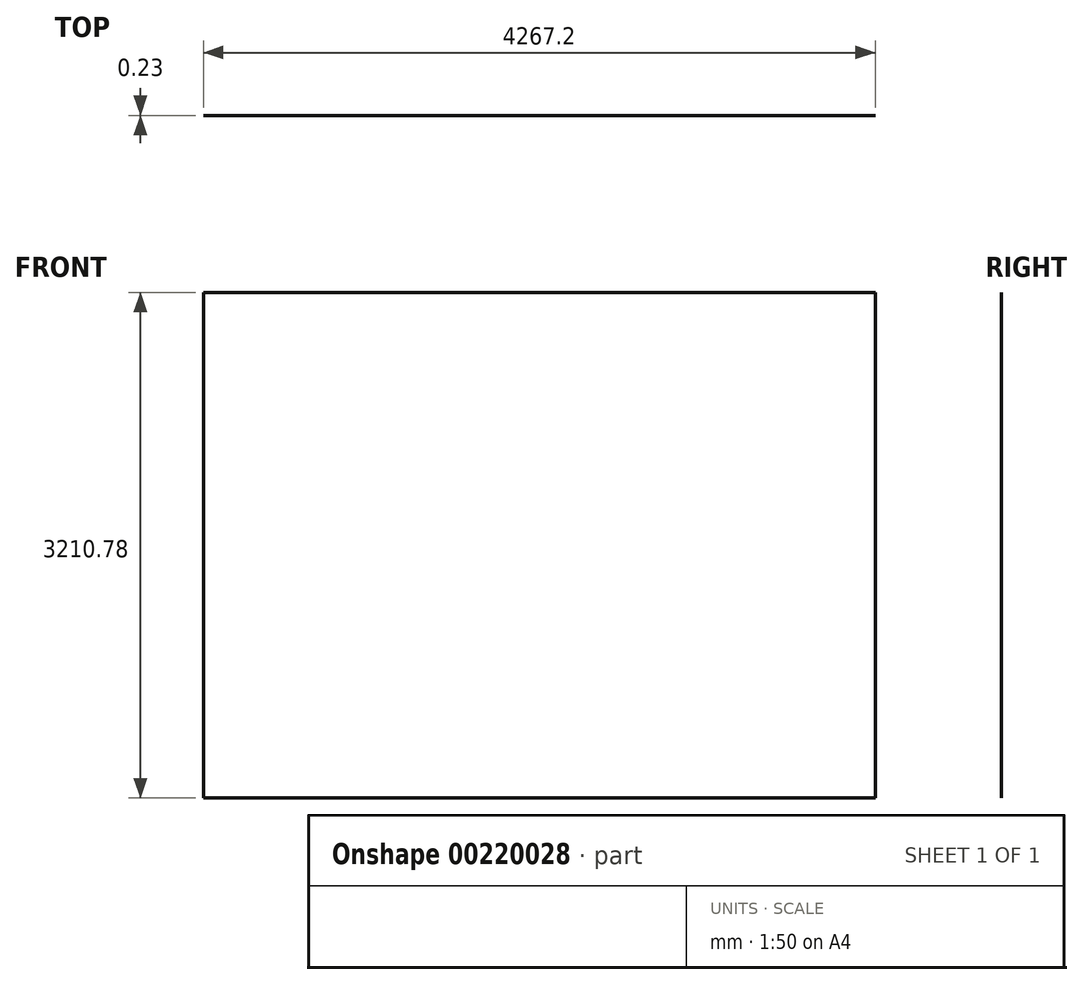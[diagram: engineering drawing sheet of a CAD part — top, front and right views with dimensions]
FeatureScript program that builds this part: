
annotation { "Feature Type Name" : "Feature", "Feature Type Description" : "" }
export const myFeature = defineFeature(function(context is Context, id is Id, definition is map)
    precondition{}
    {
        {
            var Q0;
            Q0=qCreatedBy(makeId("Front.planeOp"),FACE);
            var sketch = newSketch(context, id + "F0", { "sketchPlane" : qUnion([Q0])});
            skLineSegment(sketch, "E0.bottom", {"start": v(0, 0) * mm, "end": v(-4267.2, 0) * mm});
            skLineSegment(sketch, "E0.top", {"start": v(0, 3210.78) * mm, "end": v(-4267.2, 3210.78) * mm});
            skLineSegment(sketch, "E0.left", {"start": v(0, 0) * mm, "end": v(0, 3210.78) * mm});
            skLineSegment(sketch, "E0.right", {"start": v(-4267.2, 0) * mm, "end": v(-4267.2, 3210.78) * mm});
            skSolve(sketch);
        }
        {
            var Q0;
            Q0=makeQuery(id+"F0.imprint","IMPRINT",FACE,{"disambiguationData":[TD([[makeQuery(id+"F0.imprint","IMPRINT",EDGE,{"derivedFrom":sQuery(id+"F0.wireOp",EDGE,"E0.bottom")}),-1.0]])]});
            extrude(context, id + "F1", {"entities" : qUnion([Q0]), "depth" : 0.23 * mm});
        }
    });
